# Revit family: Lift_Incline_Garaventa_X3-Tower
name_source: partatom
category: Generic Models
units: mm (PartAtom-declared; Revit-internal decimal feet)

## family parameters
Always vertical = No
Can host rebar = No
Classification Number = 23.50.05.14.14.11
Cut with Voids When Loaded = No
Maintain Annotation Orientation = No
Part Type = Normal
Room Calculation Point = No
Round Connector Dimension = Use Diameter
Shared = No
Work Plane-Based = Yes

## types (4) — shared parameters
Assembly Code = D1010
Construction Details = http://www.arcat.com
Default Elevation = 0' - 0"
Green Building-LEED = http://www.arcat.com
Keynote = 14 42 13
Manufacturer = Garaventa Lift
Manufacturer Fax = 604-594-9915
Manufacturer Website = http://www.garaventalift.com
Product Data = http://www.arcat.com
Product Properties = http://www.garaventalift.com
Revision = R1_2017-06
Sales Information = http://www.garaventalift.com
SpecWizard = http://www.arcat.com
Specification = http://www.arcat.com
URL = http://www.garaventalift.com
Unit Depth = 0' - 2 1/2"
Unit Height = 3' - 3 3/8"
Unit Width = 0' - 2 1/2"
zero-valued in all types: Expected Lifespan (Years), Maintenance Schedule (Months), Warranty Duration (Years)

## per-type parameters (varying)
| type | Description | M Base | Model | NL Base | NR Base | T Base |
| T Base | Garaventa Lift X3 Platform T Tower Support | No | X3 T Tower Support | No | No | Yes |
| NR Base | Garaventa Lift X3 Platform NR Tower Support | No | X3 NR Tower Support | No | Yes | No |
| NL Base | Garaventa Lift X3 Platform NL Tower Support | No | X3 NL Tower Support | Yes | No | No |
| M Base | Garaventa Lift X3 Platform M Tower Support | Yes | X3 M Tower Support | No | No | No |

## geometry (parser evidence)
native form markers: Sweep x2
no freeform markers — native parametric forms only
